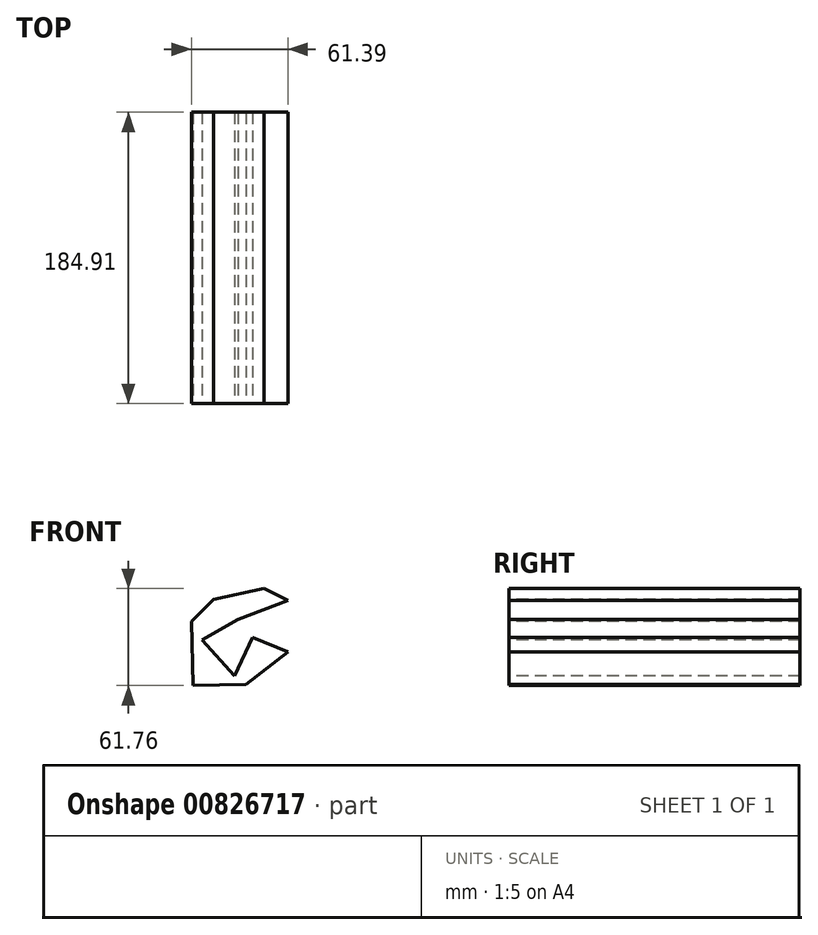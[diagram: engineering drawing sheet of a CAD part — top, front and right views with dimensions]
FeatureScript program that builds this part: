
annotation { "Feature Type Name" : "Feature", "Feature Type Description" : "" }
export const myFeature = defineFeature(function(context is Context, id is Id, definition is map)
    precondition{}
    {
        {
            var Q0;
            Q0=qCreatedBy(makeId("Front.planeOp"),FACE);
            var sketch = newSketch(context, id + "F0", { "sketchPlane" : qUnion([Q0])});
            skLineSegment(sketch, "E0", {"start": v(-29.77, 46.55) * mm, "end": v(-28.67, 5.62) * mm});
            skLineSegment(sketch, "E1", {"start": v(-28.67, 5.62) * mm, "end": v(5.05, 6.53) * mm});
            skLineSegment(sketch, "E2", {"start": v(5.05, 6.53) * mm, "end": v(31.62, 27.2) * mm});
            skLineSegment(sketch, "E3", {"start": v(31.62, 27.2) * mm, "end": v(8.94, 36.23) * mm});
            skLineSegment(sketch, "E4", {"start": v(8.94, 36.23) * mm, "end": v(-2.49, 11.7) * mm});
            skLineSegment(sketch, "E5", {"start": v(-2.49, 11.7) * mm, "end": v(-22.95, 34.75) * mm});
            skLineSegment(sketch, "E6", {"start": v(-22.95, 34.75) * mm, "end": v(0, 47.66) * mm});
            skLineSegment(sketch, "E7", {"start": v(0, 47.66) * mm, "end": v(31.62, 59.64) * mm});
            skLineSegment(sketch, "E8", {"start": v(31.62, 59.64) * mm, "end": v(16.32, 67.38) * mm});
            skLineSegment(sketch, "E9", {"start": v(16.32, 67.38) * mm, "end": v(-15.76, 60.38) * mm});
            skLineSegment(sketch, "E10", {"start": v(-15.76, 60.38) * mm, "end": v(-29.77, 46.55) * mm});
            skSolve(sketch);
        }
        {
            var Q0;
            Q0=makeQuery(id+"F0.imprint","IMPRINT",FACE,{"disambiguationData":[TD([[makeQuery(id+"F0.imprint","IMPRINT",EDGE,{"derivedFrom":sQuery(id+"F0.wireOp",EDGE,"E0")}),1.0]])]});
            extrude(context, id + "F1", {"entities" : qUnion([Q0]), "oppositeDirection" : true, "depth" : 184.9 * mm, "offsetDistance" : 25.4 * mm});
        }
    });
